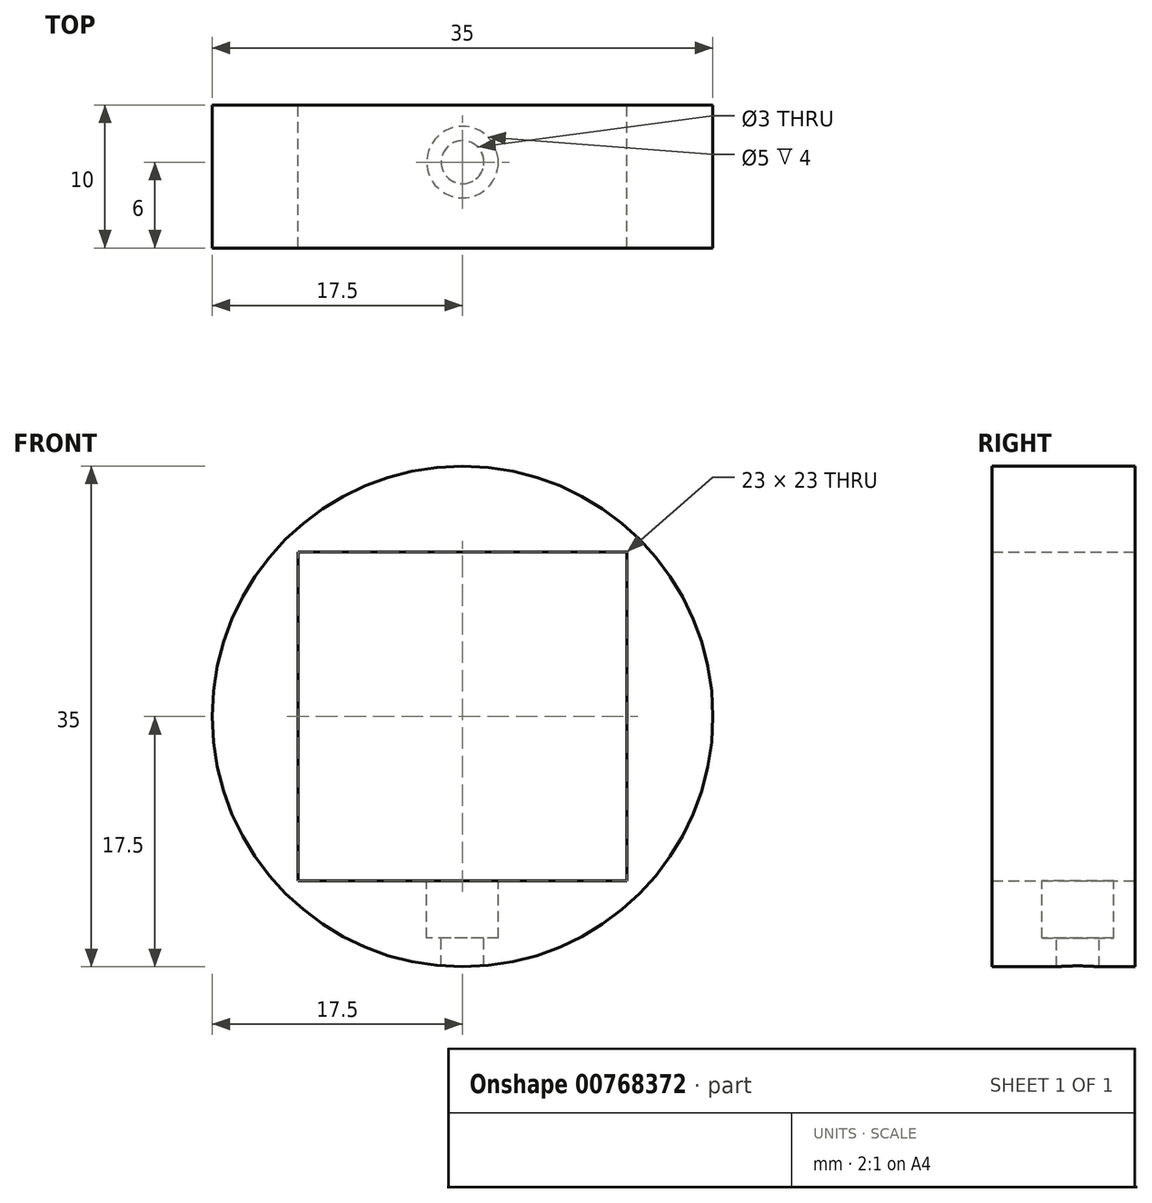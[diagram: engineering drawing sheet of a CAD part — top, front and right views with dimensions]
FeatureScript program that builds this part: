
annotation { "Feature Type Name" : "Feature", "Feature Type Description" : "" }
export const myFeature = defineFeature(function(context is Context, id is Id, definition is map)
    precondition{}
    {
        {
            var Q0;
            Q0=qCreatedBy(makeId("Front.planeOp"),FACE);
            var sketch = newSketch(context, id + "F0", { "sketchPlane" : qUnion([Q0])});
            skCircle(sketch, "E0", {"center": v(0, 0) * mm, "radius": 17.5 * mm});
            skLineSegment(sketch, "E1.bottom", {"start": v(-11.5, 11.5) * mm, "end": v(11.5, 11.5) * mm});
            skLineSegment(sketch, "E1.top", {"start": v(-11.5, -11.5) * mm, "end": v(11.5, -11.5) * mm});
            skLineSegment(sketch, "E1.left", {"start": v(-11.5, 11.5) * mm, "end": v(-11.5, -11.5) * mm});
            skLineSegment(sketch, "E1.right", {"start": v(11.5, 11.5) * mm, "end": v(11.5, -11.5) * mm});
            skSolve(sketch);
        }
        {
            var Q0;
            Q0 = qSketchRegion(id + "F0", true);
            extrude(context, id + "F1", {"entities" : qUnion([Q0]), "depth" : 10 * mm, "offsetDistance" : 25 * mm});
        }
        {
            var Q0;
            Q0=qCreatedBy(makeId("Top.planeOp"),FACE);
            var sketch = newSketch(context, id + "F2", { "sketchPlane" : qUnion([Q0])});
            skCircle(sketch, "E2", {"center": v(0, -4) * mm, "radius": 1.5 * mm});
            skSolve(sketch);
        }
        {
            var Q0;
            Q0=makeQuery(id+"F2.imprint","IMPRINT",FACE,{"disambiguationData":[TD([[makeQuery(id+"F2.imprint","IMPRINT",EDGE,{"derivedFrom":sQuery(id+"F2.wireOp",EDGE,"E2")}),1.0]])]});
            extrude(context, id + "F3", {"entities" : qUnion([Q0]), "operationType" : NewBodyOperationType.REMOVE, "oppositeDirection" : true, "depth" : 25 * mm, "offsetDistance" : 25 * mm});
        }
        {
            var Q0;
            Q0=makeQuery(id+"F1.opExtrude","SWEPT_FACE",FACE,{"disambiguationData":[OSD([sQuery(id+"F0.wireOp",EDGE,"E1.top")])]});
            var sketch = newSketch(context, id + "F4", { "sketchPlane" : qUnion([Q0])});
            skCircle(sketch, "E3", {"center": v(0, -4) * mm, "radius": 2.5 * mm});
            skSolve(sketch);
        }
        {
            var Q0;
            Q0=makeQuery(id+"F4.imprint","IMPRINT",FACE,{"disambiguationData":[TD([[makeQuery(id+"F4.imprint","IMPRINT",EDGE,{"derivedFrom":sQuery(id+"F4.wireOp",EDGE,"E3")}),1.0]])]});
            extrude(context, id + "F5", {"entities" : qUnion([Q0]), "operationType" : NewBodyOperationType.REMOVE, "oppositeDirection" : true, "depth" : 4 * mm, "offsetDistance" : 25 * mm});
        }
    });
